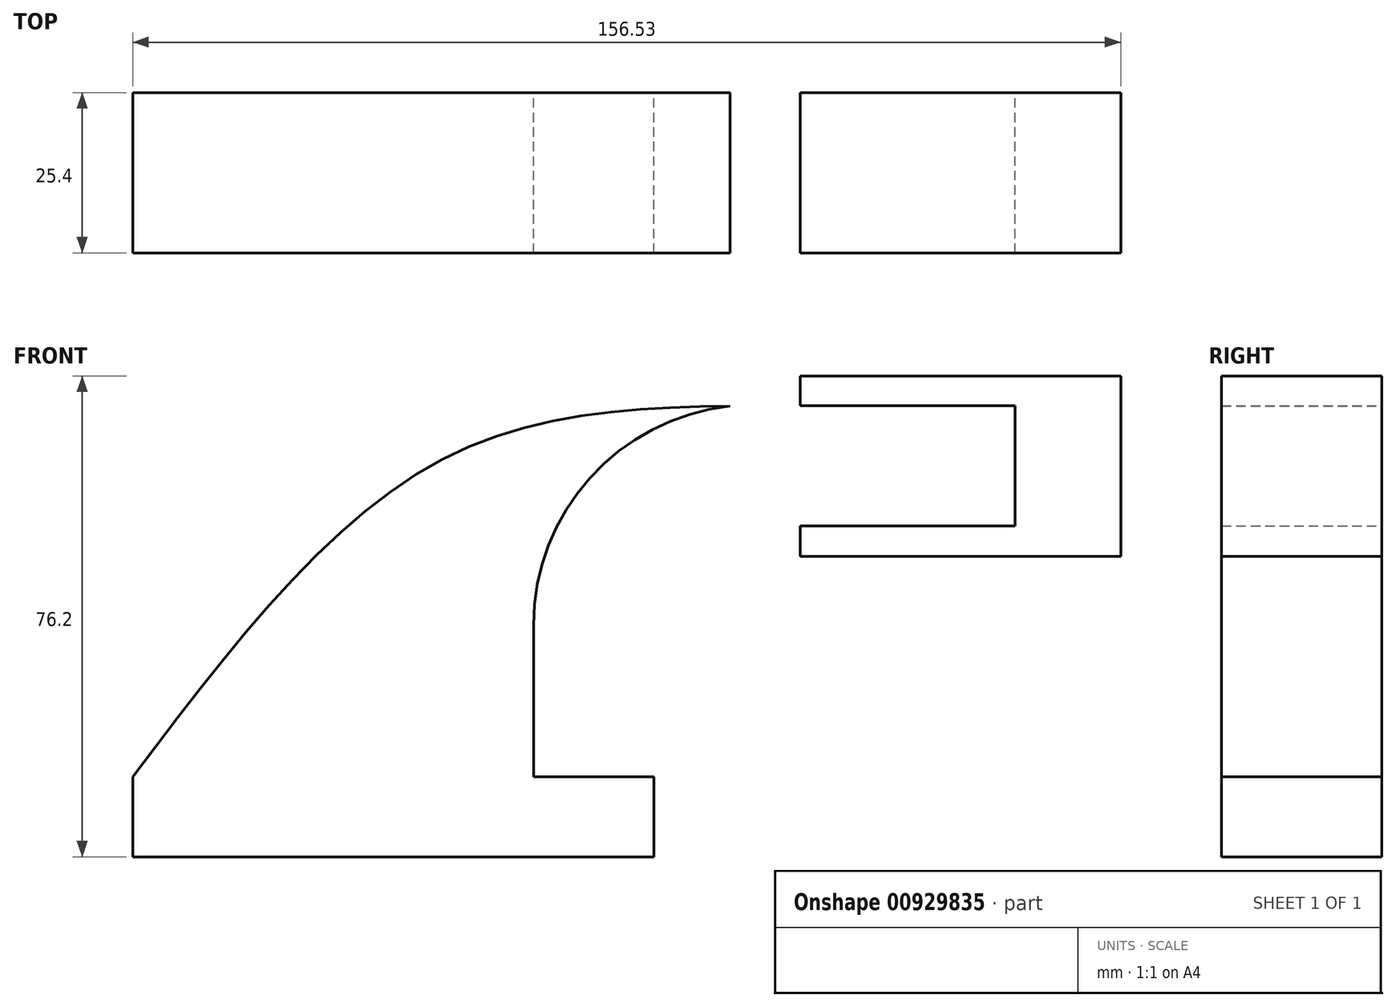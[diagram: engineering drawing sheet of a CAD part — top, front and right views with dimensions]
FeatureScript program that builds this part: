
annotation { "Feature Type Name" : "Feature", "Feature Type Description" : "" }
export const myFeature = defineFeature(function(context is Context, id is Id, definition is map)
    precondition{}
    {
        {
            var Q0;
            Q0=qCreatedBy(makeId("Front.planeOp"),FACE);
            var sketch = newSketch(context, id + "F0", { "sketchPlane" : qUnion([Q0])});
            skLineSegment(sketch, "E0.bottom", {"start": v(41.28, -6.35) * mm, "end": v(-41.28, -6.35) * mm});
            skLineSegment(sketch, "E0.top", {"start": v(41.28, 6.35) * mm, "end": v(-41.28, 6.35) * mm});
            skLineSegment(sketch, "E0.left", {"start": v(41.28, -6.35) * mm, "end": v(41.28, 6.35) * mm});
            skLineSegment(sketch, "E0.right", {"start": v(-41.28, -6.35) * mm, "end": v(-41.28, 6.35) * mm});
            skPoint(sketch, "E0.middle", {"position": v(0, 0) * mm});
            skLineSegment(sketch, "E1.bottom", {"start": v(115.25, 41.28) * mm, "end": v(64.45, 41.28) * mm});
            skLineSegment(sketch, "E1.top", {"start": v(115.25, 69.85) * mm, "end": v(64.45, 69.85) * mm});
            skLineSegment(sketch, "E1.left", {"start": v(115.25, 41.28) * mm, "end": v(115.25, 69.85) * mm});
            skLineSegment(sketch, "E1.right", {"start": v(64.45, 41.28) * mm, "end": v(64.45, 69.85) * mm});
            skPoint(sketch, "E1.middle", {"position": v(89.85, 55.56) * mm});
            skLineSegment(sketch, "E2", {"start": v(41.27, 6.35) * mm, "end": v(41.27, 30.34) * mm});
            skArc(sketch, "E3", {"start": v(41.27, 30.34) * mm, "mid": v(46.76, 42.34) * mm, "end": v(59.42, 46.05) * mm});
            skLineSegment(sketch, "E4", {"start": v(59.42, 46.05) * mm, "end": v(98.54, 46.05) * mm});
            skArc(sketch, "E5.0", {"start": v(22.22, 30.34) * mm, "mid": v(34.29, 56.74) * mm, "end": v(62.14, 64.9) * mm});
            skLineSegment(sketch, "E6.0", {"start": v(59.42, 65.1) * mm, "end": v(98.54, 65.1) * mm});
            skLineSegment(sketch, "E7.0", {"start": v(22.22, 6.35) * mm, "end": v(22.22, 30.34) * mm});
            skLineSegment(sketch, "E8", {"start": v(98.54, 46.05) * mm, "end": v(98.54, 65.1) * mm});
            skPoint(sketch, "E9.1.internal.snap0", {"position": v(34.29, 56.74) * mm});
            skFitSpline(sketch, "E9", {"points": [v(-41.28, 6.35) * mm, v(8, 56.74) * mm, v(59.42, 65.1) * mm], "startDerivative": vector(86.36, 114.05) * mm, "endDerivative": vector(115.76, 0.6) * mm});
            skSolve(sketch);
        }
        {
            var Q0;
            Q0=makeQuery(id+"F0.imprint","IMPRINT",FACE,{"disambiguationData":[TD([[makeQuery(id+"F0.imprint","IMPRINT",EDGE,{"derivedFrom":sQuery(id+"F0.wireOp",EDGE,"E0.bottom")}),-1.0]])]});
            var Q1;
            {var subQ1=sQuery(id+"F0.wireOp",EDGE,"E1.bottom");Q1=makeQuery(id+"F0.imprint","IMPRINT",FACE,{"disambiguationData":[TD([[makeQuery(id+"F0.imprint","IMPRINT",EDGE,{"derivedFrom":subQ1}),-1.0]])]});}
            var Q2;
            {var subQ3=sQuery(id+"F0.wireOp",EDGE,"E7.0");Q2=makeQuery(id+"F0.imprint","IMPRINT",FACE,{"disambiguationData":[TD([[makeQuery(id+"F0.imprint","IMPRINT",EDGE,{"derivedFrom":subQ3}),1.0]])]});}
            extrude(context, id + "F1", {"entities" : qUnion([Q0, Q1, Q2]), "depth" : 25.4 * mm, "offsetDistance" : 25.4 * mm});
        }
    });
